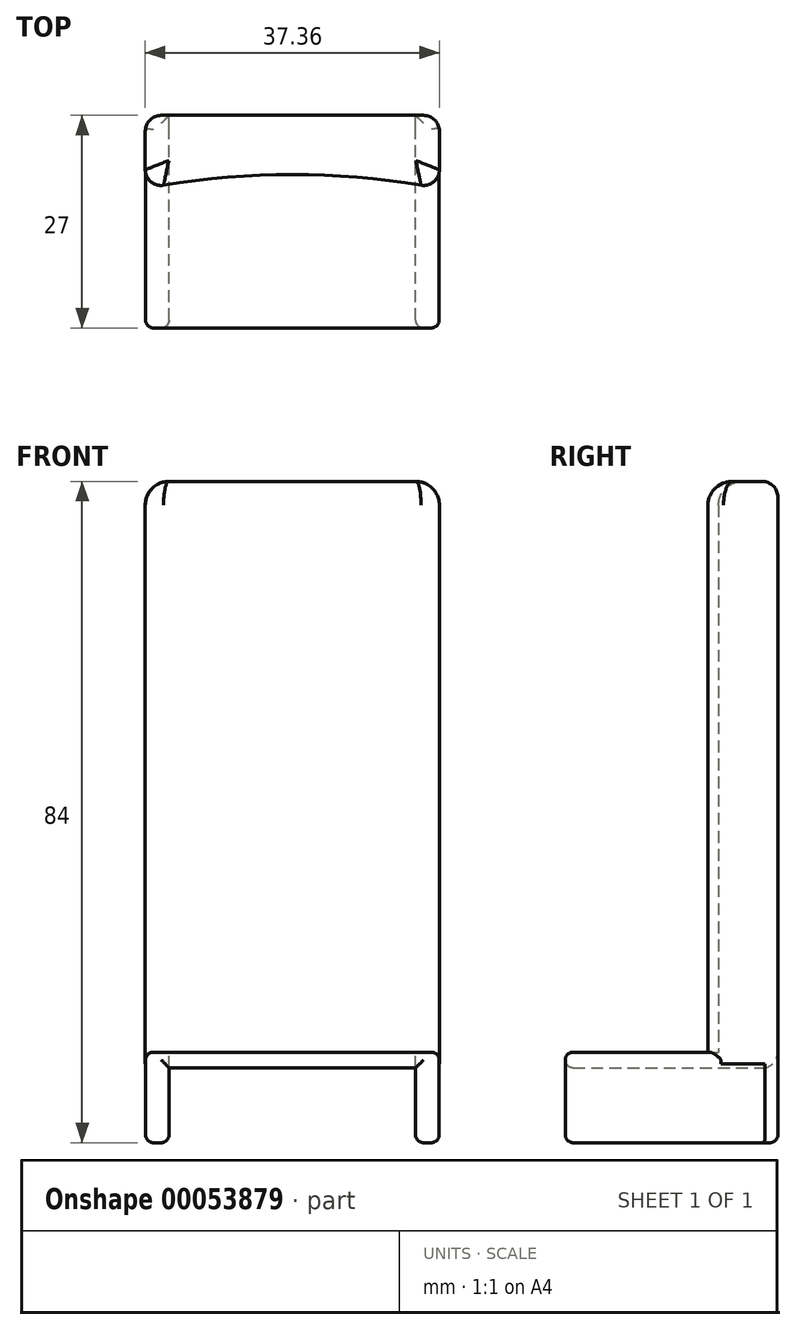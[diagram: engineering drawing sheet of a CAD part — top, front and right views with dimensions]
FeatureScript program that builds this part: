
annotation { "Feature Type Name" : "Feature", "Feature Type Description" : "" }
export const myFeature = defineFeature(function(context is Context, id is Id, definition is map)
    precondition{}
    {
        {
            var Q0;
            Q0=qCreatedBy(makeId("Front.planeOp"),FACE);
            var sketch = newSketch(context, id + "F0", { "sketchPlane" : qUnion([Q0])});
            skLineSegment(sketch, "E0.top", {"start": v(-18.65, 0) * mm, "end": v(-15.65, 0) * mm});
            skLineSegment(sketch, "E0.left", {"start": v(-18.65, 11.5) * mm, "end": v(-18.65, 0) * mm});
            skLineSegment(sketch, "E0.right", {"start": v(-15.65, 9.5) * mm, "end": v(-15.65, 0) * mm});
            skLineSegment(sketch, "E1.bottom", {"start": v(-15.65, 9.5) * mm, "end": v(0, 9.5) * mm});
            skLineSegment(sketch, "E1.top", {"start": v(-18.65, 11.5) * mm, "end": v(0, 11.5) * mm});
            skLineSegment(sketch, "E2.MirrorCS", {"start": v(15.65, 9.5) * mm, "end": v(15.65, 0) * mm});
            skLineSegment(sketch, "E3.MirrorCS", {"start": v(18.65, 11.5) * mm, "end": v(18.65, 0) * mm});
            skLineSegment(sketch, "E4.MirrorCS", {"start": v(15.65, 9.5) * mm, "end": v(0, 9.5) * mm});
            skLineSegment(sketch, "E5.MirrorCS", {"start": v(18.65, 11.5) * mm, "end": v(0, 11.5) * mm});
            skLineSegment(sketch, "E6.MirrorCS", {"start": v(18.65, 0) * mm, "end": v(15.65, 0) * mm});
            skSolve(sketch);
        }
        {
            var Q0;
            Q0=makeQuery(id+"F0.imprint","IMPRINT",FACE,{"disambiguationData":[TD([[makeQuery(id+"F0.imprint","IMPRINT",EDGE,{"derivedFrom":sQuery(id+"F0.wireOp",EDGE,"E0.top")}),1.0]])]});
            extrude(context, id + "F1", {"entities" : qUnion([Q0]), "depth" : 27 * mm});
        }
        {
            var Q0;
            Q0=qCreatedBy(makeId("Top.planeOp"),FACE);
            var sketch = newSketch(context, id + "F2", { "sketchPlane" : qUnion([Q0])});
            skLineSegment(sketch, "E7", {"start": v(-18.68, 0) * mm, "end": v(-18.68, -6.9) * mm});
            skLineSegment(sketch, "E8", {"start": v(-18.68, 0) * mm, "end": v(0, 0) * mm});
            skLineSegment(sketch, "E9.MirrorCS", {"start": v(18.68, 0) * mm, "end": v(0, 0) * mm});
            skLineSegment(sketch, "E10.MirrorCS", {"start": v(18.68, 0) * mm, "end": v(18.68, -6.9) * mm});
            skArc(sketch, "E11", {"start": v(16.35, -8.88) * mm, "mid": v(0, -7.53) * mm, "end": v(-16.35, -8.88) * mm});
            skPoint(sketch, "E12.visualSharp", {"position": v(-18.68, -9.3) * mm});
            skArc(sketch, "E12.filletArc", {"start": v(-18.68, -6.9) * mm, "mid": v(-17.97, -8.43) * mm, "end": v(-16.35, -8.88) * mm});
            skPoint(sketch, "E13.visualSharp", {"position": v(18.68, -9.3) * mm});
            skArc(sketch, "E13.filletArc", {"start": v(16.35, -8.88) * mm, "mid": v(17.97, -8.43) * mm, "end": v(18.68, -6.9) * mm});
            skSolve(sketch);
        }
        {
            var Q0;
            Q0=makeQuery(id+"F2.imprint","IMPRINT",FACE,{"disambiguationData":[TD([[makeQuery(id+"F2.imprint","IMPRINT",EDGE,{"derivedFrom":sQuery(id+"F2.wireOp",EDGE,"E7")}),1.0]])]});
            extrude(context, id + "F3", {"entities" : qUnion([Q0]), "operationType" : NewBodyOperationType.ADD, "depth" : 84 * mm, "hasSecondDirection" : true, "secondDirectionOppositeDirection" : false, "secondDirectionDepth" : 10 * mm});
        }
        {
            var Q0;
            Q0=makeQuery(id+"F3.opExtrude","SWEPT_EDGE",EDGE,{"disambiguationData":[OSD([sQuery(id+"F2.wireOp",EDGE,"E9.MirrorCS"),sQuery(id+"F2.wireOp",EDGE,"E10.MirrorCS")])]});
            var Q1;
            Q1=makeQuery(id+"F3.opExtrude","SWEPT_EDGE",EDGE,{"disambiguationData":[OSD([sQuery(id+"F2.wireOp",EDGE,"E7"),sQuery(id+"F2.wireOp",EDGE,"E8")])]});
            var Q2;
            Q2=makeQuery(id+"F3.opExtrude","CAP_EDGE",EDGE,{"disambiguationData":[OSD([sQuery(id+"F2.wireOp",EDGE,"E8"),sQuery(id+"F2.wireOp",EDGE,"E9.MirrorCS")])],"isStart":false});
            var Q3;
            Q3=makeQuery(id+"F1.opExtrude","CAP_EDGE",EDGE,{"disambiguationData":[OSD([sQuery(id+"F0.wireOp",EDGE,"E1.bottom"),sQuery(id+"F0.wireOp",EDGE,"E4.MirrorCS")])],"isStart":true});
            fillet(context, id + "F4", {"entities" : qUnion([Q0, Q1, Q2, Q3]), "radius" : 2 * mm, "tangentPropagation" : true, "allowEdgeOverflow" : false});
        }
        {
            var Q0;
            Q0=makeQuery(id+"F3.opExtrude","CAP_FACE",FACE,{"disambiguationData":[OSD([sQuery(id+"F2.wireOp",EDGE,"E7"),sQuery(id+"F2.wireOp",EDGE,"E8"),sQuery(id+"F2.wireOp",EDGE,"E9.MirrorCS"),sQuery(id+"F2.wireOp",EDGE,"E10.MirrorCS"),sQuery(id+"F2.wireOp",EDGE,"E11"),sQuery(id+"F2.wireOp",EDGE,"E12.filletArc"),sQuery(id+"F2.wireOp",EDGE,"E13.filletArc")])],"isStart":false});
            fillet(context, id + "F5", {"entities" : qUnion([Q0]), "radius" : 3 * mm, "tangentPropagation" : true, "allowEdgeOverflow" : false});
        }
        {
            var Q0;
            Q0=makeQuery(id+"F1.opExtrude","SWEPT_EDGE",EDGE,{"disambiguationData":[OSD([sQuery(id+"F0.wireOp",EDGE,"E3.MirrorCS"),sQuery(id+"F0.wireOp",EDGE,"E5.MirrorCS")])]});
            var Q1;
            Q1=makeQuery(id+"F1.opExtrude","SWEPT_EDGE",EDGE,{"disambiguationData":[OSD([sQuery(id+"F0.wireOp",EDGE,"E0.left"),sQuery(id+"F0.wireOp",EDGE,"E1.top")])]});
            var Q2;
            Q2=makeQuery(id+"F1.opExtrude","SWEPT_EDGE",EDGE,{"disambiguationData":[OSD([sQuery(id+"F0.wireOp",EDGE,"E0.top"),sQuery(id+"F0.wireOp",EDGE,"E0.left")])]});
            var Q3;
            Q3=makeQuery(id+"F1.opExtrude","CAP_EDGE",EDGE,{"disambiguationData":[OSD([sQuery(id+"F0.wireOp",EDGE,"E1.top"),sQuery(id+"F0.wireOp",EDGE,"E5.MirrorCS")])],"isStart":false});
            var Q4;
            Q4=makeQuery(id+"F1.opExtrude","CAP_EDGE",EDGE,{"disambiguationData":[OSD([sQuery(id+"F0.wireOp",EDGE,"E2.MirrorCS")])],"isStart":false});
            var Q5;
            Q5=makeQuery(id+"F1.opExtrude","CAP_EDGE",EDGE,{"disambiguationData":[OSD([sQuery(id+"F0.wireOp",EDGE,"E1.bottom"),sQuery(id+"F0.wireOp",EDGE,"E4.MirrorCS")])],"isStart":false});
            var Q6;
            Q6=makeQuery(id+"F1.opExtrude","CAP_EDGE",EDGE,{"disambiguationData":[OSD([sQuery(id+"F0.wireOp",EDGE,"E0.right")])],"isStart":false});
            var Q7;
            Q7=makeQuery(id+"F1.opExtrude","CAP_EDGE",EDGE,{"disambiguationData":[OSD([sQuery(id+"F0.wireOp",EDGE,"E3.MirrorCS")])],"isStart":false});
            var Q8;
            Q8=makeQuery(id+"F1.opExtrude","SWEPT_EDGE",EDGE,{"disambiguationData":[OSD([sQuery(id+"F0.wireOp",EDGE,"E3.MirrorCS"),sQuery(id+"F0.wireOp",EDGE,"E6.MirrorCS")])]});
            var Q9;
            Q9=makeQuery(id+"F1.opExtrude","SWEPT_EDGE",EDGE,{"disambiguationData":[OSD([sQuery(id+"F0.wireOp",EDGE,"E2.MirrorCS"),sQuery(id+"F0.wireOp",EDGE,"E6.MirrorCS")])]});
            var Q10;
            Q10=makeQuery(id+"F1.opExtrude","SWEPT_EDGE",EDGE,{"disambiguationData":[OSD([sQuery(id+"F0.wireOp",EDGE,"E0.top"),sQuery(id+"F0.wireOp",EDGE,"E0.right")])]});
            var Q11;
            Q11=makeQuery(id+"F1.opExtrude","CAP_EDGE",EDGE,{"disambiguationData":[OSD([sQuery(id+"F0.wireOp",EDGE,"E0.left")])],"isStart":false});
            var Q12;
            Q12=makeQuery(id+"F1.opExtrude","CAP_EDGE",EDGE,{"disambiguationData":[OSD([sQuery(id+"F0.wireOp",EDGE,"E6.MirrorCS")])],"isStart":false});
            var Q13;
            Q13=makeQuery(id+"F1.opExtrude","CAP_EDGE",EDGE,{"disambiguationData":[OSD([sQuery(id+"F0.wireOp",EDGE,"E0.top")])],"isStart":false});
            var Q14;
            Q14=makeQuery(id+"F4.opFillet","BLEND_EDGE",EDGE,{"blendedFrom":[makeQuery(id+"F3.opExtrude","SWEPT_EDGE",EDGE,{"disambiguationData":[OSD([sQuery(id+"F2.wireOp",EDGE,"E7"),sQuery(id+"F2.wireOp",EDGE,"E8")])]}),makeQuery(id+"F1.opExtrude","SWEPT_FACE",FACE,{"disambiguationData":[OSD([sQuery(id+"F0.wireOp",EDGE,"E0.top")])]})],"blendedInto":[makeQuery(id+"F1.opExtrude","SWEPT_FACE",FACE,{"disambiguationData":[OSD([sQuery(id+"F0.wireOp",EDGE,"E0.top")])]})]});
            var Q15;
            Q15=makeQuery(id+"F4.opFillet","BLEND_EDGE",EDGE,{"blendedFrom":[makeQuery(id+"F3.opExtrude","SWEPT_EDGE",EDGE,{"disambiguationData":[OSD([sQuery(id+"F2.wireOp",EDGE,"E9.MirrorCS"),sQuery(id+"F2.wireOp",EDGE,"E10.MirrorCS")])]}),makeQuery(id+"F1.opExtrude","SWEPT_FACE",FACE,{"disambiguationData":[OSD([sQuery(id+"F0.wireOp",EDGE,"E6.MirrorCS")])]})],"blendedInto":[makeQuery(id+"F1.opExtrude","SWEPT_FACE",FACE,{"disambiguationData":[OSD([sQuery(id+"F0.wireOp",EDGE,"E6.MirrorCS")])]})]});
            fillet(context, id + "F6", {"entities" : qUnion([Q0, Q1, Q2, Q3, Q4, Q5, Q6, Q7, Q8, Q9, Q10, Q11, Q12, Q13, Q14, Q15]), "radius" : 1 * mm, "tangentPropagation" : true, "allowEdgeOverflow" : false});
        }
    });
